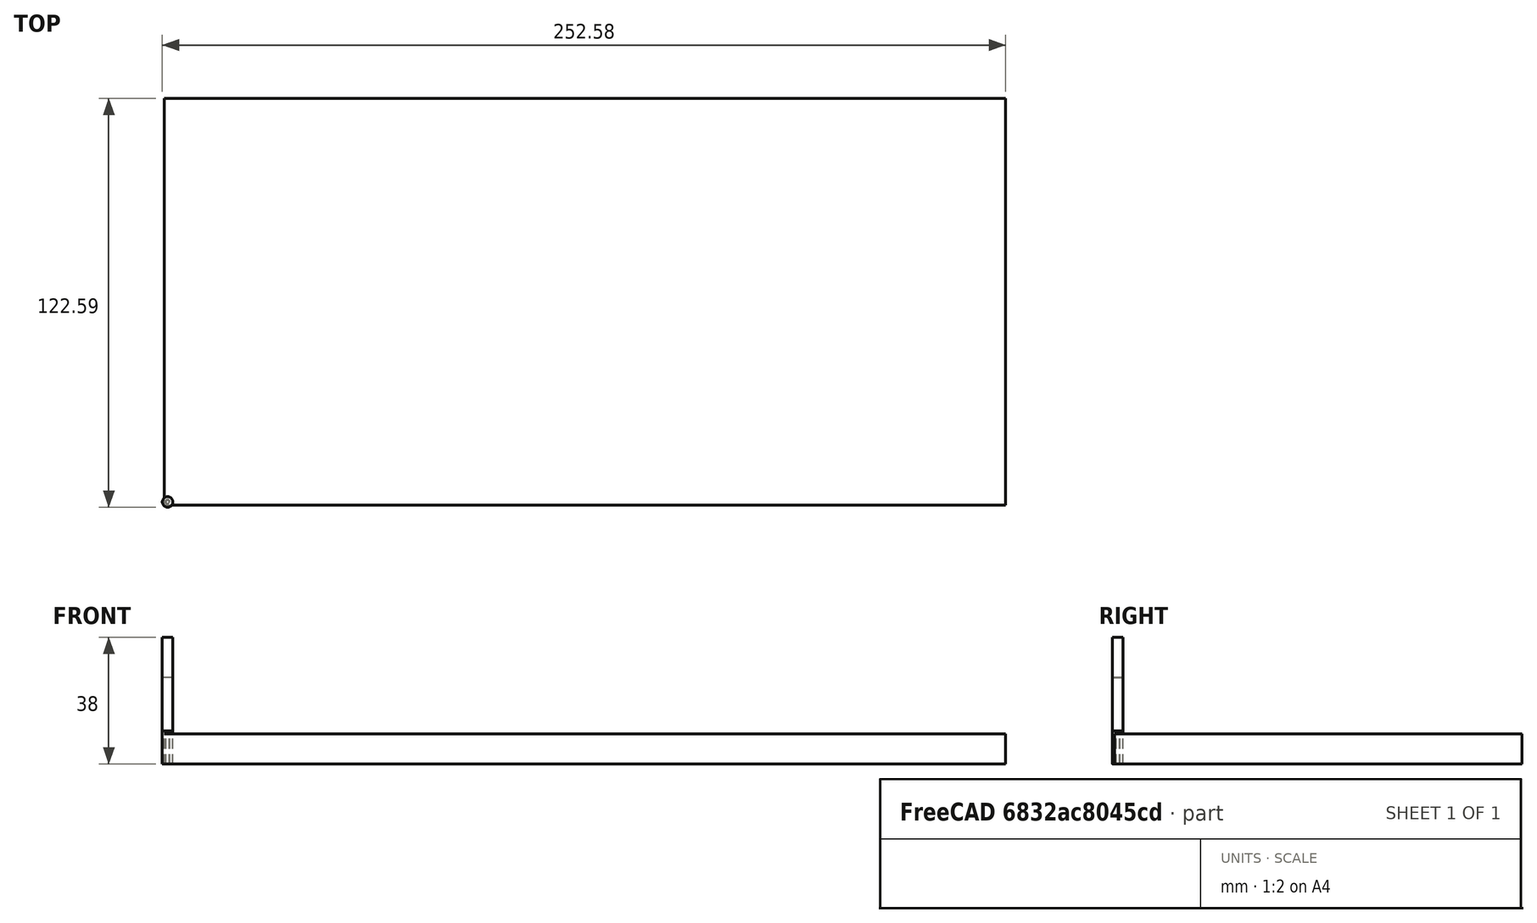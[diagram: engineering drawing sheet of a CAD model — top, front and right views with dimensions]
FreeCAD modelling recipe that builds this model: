
FCSTD DOCUMENT  (FreeCAD 0.21R33694 (Git))
Label: OIPT
License: Creative Commons Attribution 4.0
LicenseURL: https://creativecommons.org/licenses/by/4.0/
objects: Path::FeaturePython×22, Part::FeaturePython×20, App::DocumentObjectGroup×12, Part::Part2DObjectPython×4, Part::Extrusion×4, App::FeaturePython×4, Mesh::FeaturePython×2, PartDesign::AdditiveBox×1, PartDesign::SubtractiveBox×1, PartDesign::Body×1, Part::MultiFuse×1
note: 40 computed .brp shape members not serialized (recipe doc carries the construction recipe); baked Part::Feature solids carry a one-line shape summary decoded from their .brp

FEATURE [PartDesign::AdditiveBox] Box
  AttacherType = Attacher::AttachEngine3D
  Height = 9.1
  Length = 250
  MapMode = 5
  Support = -> [XY_Plane]
  Width = 120
FEATURE [Part::Part2DObjectPython] ShapeString  # Draft 2D object (typed FeaturePython)
  FontFile = /Library/Fonts/Arial Unicode.ttf
  Fuse = false
  Justification = 1
  JustificationReference = 0
  KeepLeftMargin = false
  MakeFace = true
  ObliqueAngle = 0
  Placement = pos=(43.8,91,7.1) rot=(0,0,1;0rad)
  ScaleToSize = true
  Size = 23
  String = ON PREMISE
  Tracking = 0
  expr: .Placement.Base.z = Box.Height - Box001.Height
FEATURE [Part::Part2DObjectPython] ShapeString001  # Draft 2D object (typed FeaturePython)
  FontFile = /Library/Fonts/Arial Unicode.ttf
  Fuse = false
  Justification = 1
  JustificationReference = 0
  KeepLeftMargin = false
  MakeFace = true
  ObliqueAngle = 0
  Placement = pos=(6.5,64,7.1) rot=(0,0,1;0rad)
  ScaleToSize = true
  Size = 23
  String = INFRASTRUCTURE
  Tracking = 0
  expr: .Placement.Base.z = Box.Height - Box001.Height
FEATURE [Part::Part2DObjectPython] ShapeString002  # Draft 2D object (typed FeaturePython)
  FontFile = /Library/Fonts/Arial Unicode.ttf
  Fuse = false
  Justification = 1
  JustificationReference = 0
  KeepLeftMargin = false
  MakeFace = true
  ObliqueAngle = 0
  Placement = pos=(52.45,37,7.1) rot=(0,0,1;0rad)
  ScaleToSize = true
  Size = 23
  String = PRODUCTS
  Tracking = 0
  expr: .Placement.Base.z = Box.Height - Box001.Height
FEATURE [PartDesign::SubtractiveBox] Box001
  AttacherType = Attacher::AttachEngine3D
  AttachmentOffset = pos=(5,5,-2) rot=(0,0,1;0rad)
  BaseFeature = -> Box
  Height = 2
  Length = 240
  MapMode = 5
  Placement = pos=(5,5,7.1) rot=(0,0,1;0rad)
  Support = -> [Box]
  Width = 110
  expr: .AttachmentOffset.Base.x = (Box.Length - Length) / 2
  expr: .AttachmentOffset.Base.y = (Box.Width - Width) / 2
  expr: .AttachmentOffset.Base.z = -Height
  expr: Length = Box.Length - 10 mm
  expr: Width = Box.Width - 10 mm
FEATURE [PartDesign::Body] Body
  Group = -> [Box,Box001]
  Origin = -> Origin
  Tip = -> Box001
FEATURE [Part::Part2DObjectPython] ShapeString003  # Draft 2D object (typed FeaturePython)
  FontFile = /Library/Fonts/Arial Unicode.ttf
  MakeFace = true
  Placement = pos=(81,12,7.1) rot=(-1e-06,0,1.00003;4e-06rad)
  Size = 23
  String = TEAM
  Tracking = 0
  expr: .Placement.Base.z = Box.Height - Box001.Height
FEATURE [Part::Extrusion] Extrude
  Base = -> ShapeString
  Dir = (0,0,1)
  DirMode = 2
  FaceMakerClass = Part::FaceMakerBullseye
  LengthFwd = 2
  LengthRev = 0
  Solid = true
  Symmetric = false
FEATURE [Part::Extrusion] Extrude001
  Base = -> ShapeString001
  Dir = (0,0,1)
  DirMode = 2
  FaceMakerClass = Part::FaceMakerBullseye
  LengthFwd = 2
  LengthRev = 0
  Solid = true
  Symmetric = false
FEATURE [Part::Extrusion] Extrude002
  Base = -> ShapeString002
  Dir = (0,0,1)
  DirMode = 2
  FaceMakerClass = Part::FaceMakerBullseye
  LengthFwd = 2
  LengthRev = 0
  Solid = true
  Symmetric = false
FEATURE [Part::Extrusion] Extrude003
  Base = -> ShapeString003
  Dir = (8.314e-13,2.7675e-12,1)
  DirMode = 2
  FaceMakerClass = Part::FaceMakerBullseye
  LengthFwd = 2
  LengthRev = 0
  Solid = true
  Symmetric = false
FEATURE [Part::MultiFuse] Fusion
  Shapes = -> [Body,Extrude,Extrude001,Extrude002,Extrude003]
FEATURE [App::FeaturePython] SetupSheet  # Path/CAM operation (typed FeaturePython)
  ClearanceHeightExpression = OpStockZMax+SetupSheet.ClearanceHeightOffset
  ClearanceHeightOffset = 5
  CoolantMode = 0
  CoolantModes = None | Flood | Mist
  FinalDepthExpression = OpFinalDepth
  HorizRapid = 0
  SafeHeightExpression = OpStockZMax+SetupSheet.SafeHeightOffset
  SafeHeightOffset = 3
  StartDepthExpression = OpStartDepth
  StepDownExpression = OpToolDiameter
  VertRapid = 0
FEATURE [Part::FeaturePython] Clone  label="Model-Fusion"  # Draft clone (typed FeaturePython)
  AttacherType = Attacher::AttachEngine3D
  Fuse = false
  Objects = -> [Fusion]
  PathResource = Model
  Scale = (1,1,1)
FEATURE [App::DocumentObjectGroup] Model
  Group = -> [Clone]
FEATURE [Part::FeaturePython] ToolBit  label="1.0mm-endmill"  # Path/CAM toolbit (typed FeaturePython)
  BitPropertyNames = Chipload | CuttingEdgeHeight | Diameter | Flutes | Length | Material | ShankDiameter | SpindleDirection
  BitShape = /Applications/FreeCAD.app/Contents/Resources/Mod/Path/Tools/Shape/endmill.fcstd
  Chipload = 0
  CuttingEdgeHeight = 10
  Diameter = 1
  Flutes = 0
  Length = 38
  Material = 0
  ShankDiameter = 3.17
  ShapeName = endmill
  SpindleDirection = 0
FEATURE [Path::FeaturePython] __0mm_endmill  label="1.0mm-endmill001"  # Path/CAM operation (typed FeaturePython)
  HorizFeed = 16.6667
  HorizRapid = 0
  SpindleDir = 0
  SpindleSpeed = 5000
  Tool = -> ToolBit
  ToolNumber = 5
  VertFeed = 16.6667
  VertRapid = 0
  expr: HorizRapid = SetupSheet.HorizRapid
  expr: VertRapid = SetupSheet.VertRapid
FEATURE [Part::FeaturePython] ToolBit001  label="1.4mm-endmill"  # Path/CAM toolbit (typed FeaturePython)
  BitPropertyNames = Chipload | CuttingEdgeHeight | Diameter | Flutes | Length | Material | ShankDiameter | SpindleDirection
  BitShape = /Applications/FreeCAD.app/Contents/Resources/Mod/Path/Tools/Shape/endmill.fcstd
  Chipload = 0
  CuttingEdgeHeight = 10
  Diameter = 1.4
  Flutes = 0
  Length = 26
  Material = 0
  ShankDiameter = 3
  ShapeName = endmill
  SpindleDirection = 0
FEATURE [Path::FeaturePython] __4mm_endmill  label="1.4mm-endmill001"  # Path/CAM operation (typed FeaturePython)
  HorizFeed = 16.6667
  HorizRapid = 0
  SpindleDir = 0
  SpindleSpeed = 10000
  Tool = -> ToolBit001
  ToolNumber = 2
  VertFeed = 16.6667
  VertRapid = 0
  expr: HorizRapid = SetupSheet.HorizRapid
  expr: VertRapid = SetupSheet.VertRapid
FEATURE [Part::FeaturePython] ToolBit002  label="3.175mm-endmill"  # Path/CAM toolbit (typed FeaturePython)
  BitPropertyNames = Chipload | CuttingEdgeHeight | Diameter | Flutes | Length | Material | ShankDiameter | SpindleDirection
  BitShape = /Applications/FreeCAD.app/Contents/Resources/Mod/Path/Tools/Shape/endmill.fcstd
  Chipload = 0
  CuttingEdgeHeight = 10
  Diameter = 3.17
  Flutes = 0
  Length = 26
  Material = 0
  ShankDiameter = 3
  ShapeName = endmill
  SpindleDirection = 0
FEATURE [Path::FeaturePython] __175mm_endmill  label="3.175mm-endmill001"  # Path/CAM operation (typed FeaturePython)
  HorizFeed = 16.6667
  HorizRapid = 0
  SpindleDir = 0
  SpindleSpeed = 10000
  Tool = -> ToolBit002
  ToolNumber = 4
  VertFeed = 16.6667
  VertRapid = 0
  expr: HorizRapid = SetupSheet.HorizRapid
  expr: VertRapid = SetupSheet.VertRapid
FEATURE [App::DocumentObjectGroup] Tools
  Group = -> [__0mm_endmill,__4mm_endmill,__175mm_endmill]
FEATURE [Part::FeaturePython] Stock  # WARN: FeaturePython — macro-defined, semantics opaque (R4)
  Base = -> Model
  ExtXneg = 1
  ExtXpos = 1
  ExtYneg = 1
  ExtYpos = 1
  ExtZneg = 0
  ExtZpos = 0
  StockType = FromBase
FEATURE [Path::FeaturePython] Pocket_Shape  # Path/CAM operation (typed FeaturePython)
  Active = true
  AreaParams:
    Tolerance = 1e-07
    FitArcs = True
    Simplify = False
    CleanDistance = 0.0
    Accuracy = 0.01
    Unit = 1.0
    MinArcPoints = 4
    MaxArcPoints = 100
    ClipperScale = 10000000.0
    Fill = 0
    Coplanar = 0
    Reorient = True
    Outline = False
    Explode = False
    OpenMode = 0
    Deflection = 0.01
    SubjectFill = 0
    ClipFill = 0
    Offset = 0.0
    ExtraPass = 0
    Stepover = 0.0
    LastStepover = 0.0
    JoinType = 0
    EndType = 0
    MiterLimit = 2.0
    RoundPrecision = 0.0
    PocketMode = 4
    ToolRadius = 1.585
    PocketExtraOffset = 0.0
    PocketStepover = 3.17
    PocketLastStepover = 0.0
    FromCenter = True
    Angle = 45.0
    AngleShift = 0.0
    Shift = 0.0
    Thicken = False
    SectionCount = -1
    Stepdown = 1.0
    SectionOffset = 0.0
    SectionTolerance = 1e-07
    SectionMode = 2
    Project = False
  Base = -> [Clone]
  ClearanceHeight = 14.1
  CoolantMode = 0
  CutMode = 0
  CycleTime = 00:27:07
  ExtensionCorners = true
  ExtensionLengthDefault = 1.585
  ExtraOffset = 0
  FinalDepth = 7.3
  FinishDepth = 0
  KeepToolDown = false
  MinTravel = false
  OffsetPattern = 2
  OpFinalDepth = 7.1
  OpStartDepth = 9.1
  OpStockZMax = 9.1
  OpStockZMin = 0
  OpToolDiameter = 3.17
  PathParams = {'orientation': 1, 'feedrate': 16.666666666666668, 'feedrate_v': 16.666666666666668, 'verbose': True, 'resume_height': 12.1, 'retraction': 14.1, 'return_end': True, 'preamble': False, 'start': Vector (217.01123131992824, 78.83016025976677, 14.1)}
  PocketLastStepOver = 0
  SafeHeight = 12.1
  SplitArcs = false
  StartAt = 0
  StartDepth = 9.3
  StartPoint = (0,0,0)
  StepDown = 1
  StepOver = 100
  ToolController = -> __175mm_endmill
  UseOutline = false
  UseStartPoint = false
  ZigZagAngle = 45
  expr: ClearanceHeight = OpStockZMax + SetupSheet.ClearanceHeightOffset
  expr: ExtensionLengthDefault = OpToolDiameter / 2
  expr: FinalDepth = 9.3 mm - Box001.Height
  expr: SafeHeight = OpStockZMax + SetupSheet.SafeHeightOffset
  expr: StartDepth = 9.3
  expr: StepDown = 1
FEATURE [App::DocumentObjectGroup] Operations
  Group = -> [Pocket_Shape]
FEATURE [Path::FeaturePython] Job  # Path/CAM operation (typed FeaturePython)
  CycleTime = 00:27:07
  Fixtures = G54
  GeometryTolerance = 0.01
  JobType = 0
  LastPostProcessDate = 2024-03-01 13:59:01.263896
  LastPostProcessOutput = /Volumes/NEW VOLUME/oipt1.nc
  Model = -> Model
  Operations = -> Operations
  OrderOutputBy = 0
  PostProcessor = 1
  PostProcessorOutputFile = <userpath>/3d_projects/CNC-stuff/placard/nameplate.nc
  SetupSheet = -> SetupSheet
  SplitOutput = false
  Stock = -> Stock
  Tools = -> Tools
FEATURE [Mesh::FeaturePython] CutMaterial  # WARN: FeaturePython — macro-defined, semantics opaque (R4)
FEATURE [App::FeaturePython] SetupSheet001  # Path/CAM operation (typed FeaturePython)
  ClearanceHeightExpression = OpStockZMax+SetupSheet001.ClearanceHeightOffset
  ClearanceHeightOffset = 5
  CoolantMode = 0
  CoolantModes = None | Flood | Mist
  FinalDepthExpression = OpFinalDepth
  HorizRapid = 0
  SafeHeightExpression = OpStockZMax+SetupSheet001.SafeHeightOffset
  SafeHeightOffset = 3
  StartDepthExpression = OpStartDepth
  StepDownExpression = OpToolDiameter
  VertRapid = 0
FEATURE [Part::FeaturePython] Clone001  label="Model-Fusion001"  # Draft clone (typed FeaturePython)
  AttacherType = Attacher::AttachEngine3D
  Fuse = false
  Objects = -> [Fusion]
  PathResource = Model
  Scale = (1,1,1)
FEATURE [App::DocumentObjectGroup] Model001
  Group = -> [Clone001]
FEATURE [Part::FeaturePython] ToolBit003  label="1.0mm-endmill003"  # Path/CAM toolbit (typed FeaturePython)
  BitPropertyNames = Chipload | CuttingEdgeHeight | Diameter | Flutes | Length | Material | ShankDiameter | SpindleDirection
  BitShape = /Applications/FreeCAD.app/Contents/Resources/Mod/Path/Tools/Shape/endmill.fcstd
  Chipload = 0
  CuttingEdgeHeight = 10
  Diameter = 1
  Flutes = 0
  Length = 38
  Material = 0
  ShankDiameter = 3.17
  ShapeName = endmill
  SpindleDirection = 0
FEATURE [Path::FeaturePython] __0mm_endmill001  label="1.0mm-endmill002"  # Path/CAM operation (typed FeaturePython)
  HorizFeed = 16.6667
  HorizRapid = 0
  SpindleDir = 0
  SpindleSpeed = 5000
  Tool = -> ToolBit003
  ToolNumber = 5
  VertFeed = 16.6667
  VertRapid = 0
  expr: HorizRapid = SetupSheet001.HorizRapid
  expr: VertRapid = SetupSheet001.VertRapid
FEATURE [Part::FeaturePython] ToolBit004  label="1.4mm-endmill003"  # Path/CAM toolbit (typed FeaturePython)
  BitPropertyNames = Chipload | CuttingEdgeHeight | Diameter | Flutes | Length | Material | ShankDiameter | SpindleDirection
  BitShape = /Applications/FreeCAD.app/Contents/Resources/Mod/Path/Tools/Shape/endmill.fcstd
  Chipload = 0
  CuttingEdgeHeight = 10
  Diameter = 1.4
  Flutes = 0
  Length = 26
  Material = 0
  ShankDiameter = 3
  ShapeName = endmill
  SpindleDirection = 0
FEATURE [Path::FeaturePython] __4mm_endmill001  label="1.4mm-endmill002"  # Path/CAM operation (typed FeaturePython)
  HorizFeed = 16.6667
  HorizRapid = 0
  SpindleDir = 0
  SpindleSpeed = 10000
  Tool = -> ToolBit004
  ToolNumber = 2
  VertFeed = 16.6667
  VertRapid = 0
  expr: HorizRapid = SetupSheet001.HorizRapid
  expr: VertRapid = SetupSheet001.VertRapid
FEATURE [Part::FeaturePython] ToolBit005  label="3.175mm-endmill003"  # Path/CAM toolbit (typed FeaturePython)
  BitPropertyNames = Chipload | CuttingEdgeHeight | Diameter | Flutes | Length | Material | ShankDiameter | SpindleDirection
  BitShape = /Applications/FreeCAD.app/Contents/Resources/Mod/Path/Tools/Shape/endmill.fcstd
  Chipload = 0
  CuttingEdgeHeight = 10
  Diameter = 3.17
  Flutes = 0
  Length = 26
  Material = 0
  ShankDiameter = 3
  ShapeName = endmill
  SpindleDirection = 0
FEATURE [Path::FeaturePython] __175mm_endmill001  label="3.175mm-endmill002"  # Path/CAM operation (typed FeaturePython)
  HorizFeed = 33.3333
  HorizRapid = 0
  SpindleDir = 0
  SpindleSpeed = 10000
  Tool = -> ToolBit005
  ToolNumber = 4
  VertFeed = 33.3333
  VertRapid = 0
  expr: HorizRapid = SetupSheet001.HorizRapid
  expr: VertRapid = SetupSheet001.VertRapid
FEATURE [App::DocumentObjectGroup] Tools001
  Group = -> [__0mm_endmill001,__4mm_endmill001,__175mm_endmill001]
FEATURE [Part::FeaturePython] Stock001  # WARN: FeaturePython — macro-defined, semantics opaque (R4)
  Base = -> Model001
  ExtXneg = 1
  ExtXpos = 1
  ExtYneg = 1
  ExtYpos = 1
  ExtZneg = 0
  ExtZpos = 0
  StockType = FromBase
FEATURE [Path::FeaturePython] Profile  # Path/CAM operation (typed FeaturePython)
  Active = true
  AreaParams:
    Tolerance = 1e-07
    FitArcs = True
    Simplify = False
    CleanDistance = 0.0
    Accuracy = 0.01
    Unit = 1.0
    MinArcPoints = 4
    MaxArcPoints = 100
    ClipperScale = 10000000.0
    Fill = 0
    Coplanar = 0
    Reorient = True
    Outline = False
    Explode = False
    OpenMode = 0
    Deflection = 0.01
    SubjectFill = 0
    ClipFill = 0
    Offset = 0.7
    ExtraPass = 0
    Stepover = 0.0
    LastStepover = 0.0
    JoinType = 0
    EndType = 0
    MiterLimit = 2.0
    RoundPrecision = 0.0
    PocketMode = 0
    ToolRadius = 1.0
    PocketExtraOffset = 0.0
    PocketStepover = 0.0
    PocketLastStepover = 0.0
    FromCenter = False
    Angle = 45.0
    AngleShift = 0.0
    Shift = 0.0
    Thicken = False
    SectionCount = -1
    Stepdown = 1.0
    SectionOffset = 0.0
    SectionTolerance = 1e-07
    SectionMode = 2
    Project = False
  Base = -> [Clone001]
  ClearanceHeight = 14.1
  CoolantMode = 0
  CycleTime = 00:04:38
  Direction = 0
  FinalDepth = 7.1
  HandleMultipleFeatures = 0
  JoinType = 0
  MiterLimit = 0.1
  OffsetExtra = 0
  OpFinalDepth = 7.1
  OpStartDepth = 9.1
  OpStockZMax = 9.1
  OpStockZMin = 0
  OpToolDiameter = 1.4
  PathParams = {'orientation': 0, 'feedrate': 16.666666666666668, 'feedrate_v': 16.666666666666668, 'verbose': True, 'resume_height': 12.1, 'retraction': 14.1, 'return_end': True, 'preamble': False, 'start': Vector (112.09030395670032, 21.42941604003683, 14.1)}
  SafeHeight = 12.1
  Side = 1
  SplitArcs = false
  StartDepth = 7.1
  StartPoint = (0,0,0)
  StepDown = 1.4
  ToolController = -> __4mm_endmill001
  UseComp = true
  UseStartPoint = false
  processCircles = true
  processHoles = true
  processPerimeter = true
  expr: ClearanceHeight = OpStockZMax + SetupSheet001.ClearanceHeightOffset
  expr: FinalDepth = Box.Height - Box001.Height
  expr: SafeHeight = OpStockZMax + SetupSheet001.SafeHeightOffset
  expr: StartDepth = Box.Height - Box001.Height
  expr: StepDown = OpToolDiameter
FEATURE [Path::FeaturePython] Profile001  # Path/CAM operation (typed FeaturePython)
  Active = true
  AreaParams:
    Tolerance = 1e-07
    FitArcs = True
    Simplify = False
    CleanDistance = 0.0
    Accuracy = 0.01
    Unit = 1.0
    MinArcPoints = 4
    MaxArcPoints = 100
    ClipperScale = 10000000.0
    Fill = 0
    Coplanar = 0
    Reorient = True
    Outline = False
    Explode = False
    OpenMode = 0
    Deflection = 0.01
    SubjectFill = 0
    ClipFill = 0
    Offset = -0.7
    ExtraPass = 0
    Stepover = 0.0
    LastStepover = 0.0
    JoinType = 0
    EndType = 0
    MiterLimit = 2.0
    RoundPrecision = 0.0
    PocketMode = 0
    ToolRadius = 1.0
    PocketExtraOffset = 0.0
    PocketStepover = 0.0
    PocketLastStepover = 0.0
    FromCenter = False
    Angle = 45.0
    AngleShift = 0.0
    Shift = 0.0
    Thicken = False
    SectionCount = -1
    Stepdown = 1.0
    SectionOffset = 0.0
    SectionTolerance = 1e-07
    SectionMode = 2
    Project = False
  Base = -> [Clone001]
  ClearanceHeight = 14.1
  CoolantMode = 0
  CycleTime = 00:00:59
  Direction = 0
  FinalDepth = 7.1
  HandleMultipleFeatures = 0
  JoinType = 0
  MiterLimit = 0.1
  OffsetExtra = 0
  OpFinalDepth = 7.1
  OpStartDepth = 9.1
  OpStockZMax = 9.1
  OpStockZMin = 0
  OpToolDiameter = 1.4
  PathParams = {'orientation': 1, 'feedrate': 16.666666666666668, 'feedrate_v': 16.666666666666668, 'verbose': True, 'resume_height': 12.1, 'retraction': 14.1, 'return_end': True, 'preamble': False}
  SafeHeight = 12.1
  Side = 1
  SplitArcs = false
  StartDepth = 7.1
  StartPoint = (0,0,0)
  StepDown = 1.4
  ToolController = -> __4mm_endmill001
  UseComp = true
  UseStartPoint = false
  processCircles = true
  processHoles = true
  processPerimeter = true
  expr: ClearanceHeight = OpStockZMax + SetupSheet001.ClearanceHeightOffset
  expr: FinalDepth = Box.Height - Box001.Height
  expr: SafeHeight = OpStockZMax + SetupSheet001.SafeHeightOffset
  expr: StartDepth = Box.Height - Box001.Height
  expr: StepDown = OpToolDiameter
FEATURE [App::DocumentObjectGroup] Operations001
  Group = -> [Profile,Profile001]
FEATURE [Path::FeaturePython] Job001  # Path/CAM operation (typed FeaturePython)
  CycleTime = 00:05:37
  Fixtures = G54
  GeometryTolerance = 0.01
  JobType = 0
  Model = -> Model001
  Operations = -> Operations001
  OrderOutputBy = 0
  PostProcessor = 1
  PostProcessorOutputFile = <userpath>/3d_projects/CNC-stuff/placard/nameplate.nc
  SetupSheet = -> SetupSheet001
  SplitOutput = false
  Stock = -> Stock001
  Tools = -> Tools001
FEATURE [App::FeaturePython] SetupSheet002  # Path/CAM operation (typed FeaturePython)
  ClearanceHeightExpression = OpStockZMax+SetupSheet002.ClearanceHeightOffset
  ClearanceHeightOffset = 5
  CoolantMode = 0
  CoolantModes = None | Flood | Mist
  FinalDepthExpression = OpFinalDepth
  HorizRapid = 0
  SafeHeightExpression = OpStockZMax+SetupSheet002.SafeHeightOffset
  SafeHeightOffset = 3
  StartDepthExpression = OpStartDepth
  StepDownExpression = OpToolDiameter
  VertRapid = 0
FEATURE [Part::FeaturePython] Clone002  label="Model-Fusion002"  # Draft clone (typed FeaturePython)
  AttacherType = Attacher::AttachEngine3D
  Fuse = false
  Objects = -> [Fusion]
  PathResource = Model
  Scale = (1,1,1)
FEATURE [App::DocumentObjectGroup] Model002
  Group = -> [Clone002]
FEATURE [Part::FeaturePython] ToolBit006  label="1.0mm-endmill005"  # Path/CAM toolbit (typed FeaturePython)
  BitPropertyNames = Chipload | CuttingEdgeHeight | Diameter | Flutes | Length | Material | ShankDiameter | SpindleDirection
  BitShape = /Applications/FreeCAD.app/Contents/Resources/Mod/Path/Tools/Shape/endmill.fcstd
  Chipload = 0
  CuttingEdgeHeight = 10
  Diameter = 1
  Flutes = 0
  Length = 38
  Material = 0
  ShankDiameter = 3.17
  ShapeName = endmill
  SpindleDirection = 0
FEATURE [Path::FeaturePython] __0mm_endmill002  label="1.0mm-endmill004"  # Path/CAM operation (typed FeaturePython)
  HorizFeed = 16.6667
  HorizRapid = 0
  SpindleDir = 0
  SpindleSpeed = 5000
  Tool = -> ToolBit006
  ToolNumber = 5
  VertFeed = 16.6667
  VertRapid = 0
  expr: HorizRapid = SetupSheet002.HorizRapid
  expr: VertRapid = SetupSheet002.VertRapid
FEATURE [Part::FeaturePython] ToolBit007  label="1.4mm-endmill005"  # Path/CAM toolbit (typed FeaturePython)
  BitPropertyNames = Chipload | CuttingEdgeHeight | Diameter | Flutes | Length | Material | ShankDiameter | SpindleDirection
  BitShape = /Applications/FreeCAD.app/Contents/Resources/Mod/Path/Tools/Shape/endmill.fcstd
  Chipload = 0
  CuttingEdgeHeight = 10
  Diameter = 1.4
  Flutes = 0
  Length = 26
  Material = 0
  ShankDiameter = 3
  ShapeName = endmill
  SpindleDirection = 0
FEATURE [Path::FeaturePython] __4mm_endmill002  label="1.4mm-endmill004"  # Path/CAM operation (typed FeaturePython)
  HorizFeed = 16.6667
  HorizRapid = 0
  SpindleDir = 0
  SpindleSpeed = 10000
  Tool = -> ToolBit007
  ToolNumber = 2
  VertFeed = 16.6667
  VertRapid = 0
  expr: HorizRapid = SetupSheet002.HorizRapid
  expr: VertRapid = SetupSheet002.VertRapid
FEATURE [Part::FeaturePython] ToolBit008  label="3.175mm-endmill005"  # Path/CAM toolbit (typed FeaturePython)
  BitPropertyNames = Chipload | CuttingEdgeHeight | Diameter | Flutes | Length | Material | ShankDiameter | SpindleDirection
  BitShape = /Applications/FreeCAD.app/Contents/Resources/Mod/Path/Tools/Shape/endmill.fcstd
  Chipload = 0
  CuttingEdgeHeight = 10
  Diameter = 3.17
  Flutes = 0
  Length = 26
  Material = 0
  ShankDiameter = 3
  ShapeName = endmill
  SpindleDirection = 0
FEATURE [Path::FeaturePython] __175mm_endmill002  label="3.175mm-endmill004"  # Path/CAM operation (typed FeaturePython)
  HorizFeed = 33.3333
  HorizRapid = 0
  SpindleDir = 0
  SpindleSpeed = 10000
  Tool = -> ToolBit008
  ToolNumber = 4
  VertFeed = 33.3333
  VertRapid = 0
  expr: HorizRapid = SetupSheet002.HorizRapid
  expr: VertRapid = SetupSheet002.VertRapid
FEATURE [App::DocumentObjectGroup] Tools002
  Group = -> [__0mm_endmill002,__4mm_endmill002,__175mm_endmill002]
FEATURE [Part::FeaturePython] Stock002  # WARN: FeaturePython — macro-defined, semantics opaque (R4)
  Base = -> Model002
  ExtXneg = 1
  ExtXpos = 1
  ExtYneg = 1
  ExtYpos = 1
  ExtZneg = 0
  ExtZpos = 0
  StockType = FromBase
FEATURE [Path::FeaturePython] Profile002  # Path/CAM operation (typed FeaturePython)
  Active = true
  AreaParams:
    Tolerance = 1e-07
    FitArcs = True
    Simplify = False
    CleanDistance = 0.0
    Accuracy = 0.01
    Unit = 1.0
    MinArcPoints = 4
    MaxArcPoints = 100
    ClipperScale = 10000000.0
    Fill = 0
    Coplanar = 0
    Reorient = True
    Outline = False
    Explode = False
    OpenMode = 0
    Deflection = 0.01
    SubjectFill = 0
    ClipFill = 0
    Offset = 0.5
    ExtraPass = 0
    Stepover = 0.0
    LastStepover = 0.0
    JoinType = 0
    EndType = 0
    MiterLimit = 2.0
    RoundPrecision = 0.0
    PocketMode = 0
    ToolRadius = 1.0
    PocketExtraOffset = 0.0
    PocketStepover = 0.0
    PocketLastStepover = 0.0
    FromCenter = False
    Angle = 45.0
    AngleShift = 0.0
    Shift = 0.0
    Thicken = False
    SectionCount = -1
    Stepdown = 1.0
    SectionOffset = 0.0
    SectionTolerance = 1e-07
    SectionMode = 2
    Project = False
  Base = -> [Clone002]
  ClearanceHeight = 14.1
  CoolantMode = 0
  CycleTime = 00:04:38
  Direction = 0
  FinalDepth = 7.1
  HandleMultipleFeatures = 0
  JoinType = 0
  MiterLimit = 0.1
  OffsetExtra = 0
  OpFinalDepth = 7.1
  OpStartDepth = 9.1
  OpStockZMax = 9.1
  OpStockZMin = 0
  OpToolDiameter = 1
  PathParams = {'orientation': 0, 'feedrate': 16.666666666666668, 'feedrate_v': 16.666666666666668, 'verbose': True, 'resume_height': 12.1, 'retraction': 14.1, 'return_end': True, 'preamble': False, 'start': Vector (111.89030443104416, 21.313495172891262, 14.1)}
  SafeHeight = 12.1
  Side = 1
  SplitArcs = false
  StartDepth = 7.1
  StartPoint = (0,0,0)
  StepDown = 1
  ToolController = -> __0mm_endmill002
  UseComp = true
  UseStartPoint = false
  processCircles = true
  processHoles = true
  processPerimeter = true
  expr: ClearanceHeight = OpStockZMax + SetupSheet002.ClearanceHeightOffset
  expr: FinalDepth = Box.Height - Box001.Height
  expr: SafeHeight = OpStockZMax + SetupSheet002.SafeHeightOffset
  expr: StartDepth = Box.Height - Box001.Height
  expr: StepDown = OpToolDiameter
FEATURE [Path::FeaturePython] Profile003  # Path/CAM operation (typed FeaturePython)
  Active = true
  AreaParams:
    Tolerance = 1e-07
    FitArcs = True
    Simplify = False
    CleanDistance = 0.0
    Accuracy = 0.01
    Unit = 1.0
    MinArcPoints = 4
    MaxArcPoints = 100
    ClipperScale = 10000000.0
    Fill = 0
    Coplanar = 0
    Reorient = True
    Outline = False
    Explode = False
    OpenMode = 0
    Deflection = 0.01
    SubjectFill = 0
    ClipFill = 0
    Offset = -0.5
    ExtraPass = 0
    Stepover = 0.0
    LastStepover = 0.0
    JoinType = 0
    EndType = 0
    MiterLimit = 2.0
    RoundPrecision = 0.0
    PocketMode = 0
    ToolRadius = 1.0
    PocketExtraOffset = 0.0
    PocketStepover = 0.0
    PocketLastStepover = 0.0
    FromCenter = False
    Angle = 45.0
    AngleShift = 0.0
    Shift = 0.0
    Thicken = False
    SectionCount = -1
    Stepdown = 1.0
    SectionOffset = 0.0
    SectionTolerance = 1e-07
    SectionMode = 2
    Project = False
  Base = -> [Clone002]
  ClearanceHeight = 14.1
  CoolantMode = 0
  CycleTime = 00:00:59
  Direction = 0
  FinalDepth = 7.1
  HandleMultipleFeatures = 0
  JoinType = 0
  MiterLimit = 0.1
  OffsetExtra = 0
  OpFinalDepth = 7.1
  OpStartDepth = 9.1
  OpStockZMax = 9.1
  OpStockZMin = 0
  OpToolDiameter = 1
  PathParams = {'orientation': 1, 'feedrate': 16.666666666666668, 'feedrate_v': 16.666666666666668, 'verbose': True, 'resume_height': 12.1, 'retraction': 14.1, 'return_end': True, 'preamble': False}
  SafeHeight = 12.1
  Side = 1
  SplitArcs = false
  StartDepth = 7.1
  StartPoint = (0,0,0)
  StepDown = 1
  ToolController = -> __0mm_endmill002
  UseComp = true
  UseStartPoint = false
  processCircles = false
  processHoles = false
  processPerimeter = true
  expr: ClearanceHeight = OpStockZMax + SetupSheet002.ClearanceHeightOffset
  expr: FinalDepth = Box.Height - Box001.Height
  expr: SafeHeight = OpStockZMax + SetupSheet002.SafeHeightOffset
  expr: StartDepth = Box.Height - Box001.Height
  expr: StepDown = OpToolDiameter
FEATURE [App::DocumentObjectGroup] Operations002
  Group = -> [Profile002,Profile003]
FEATURE [Path::FeaturePython] Job002  # Path/CAM operation (typed FeaturePython)
  CycleTime = 00:05:37
  Fixtures = G54
  GeometryTolerance = 0.01
  JobType = 0
  Model = -> Model002
  Operations = -> Operations002
  OrderOutputBy = 0
  PostProcessor = 1
  PostProcessorOutputFile = <userpath>/3d_projects/CNC-stuff/placard/nameplate.nc
  SetupSheet = -> SetupSheet002
  SplitOutput = false
  Stock = -> Stock002
  Tools = -> Tools002
FEATURE [App::FeaturePython] SetupSheet003  # Path/CAM operation (typed FeaturePython)
  ClearanceHeightExpression = OpStockZMax+SetupSheet003.ClearanceHeightOffset
  ClearanceHeightOffset = 5
  CoolantMode = 0
  CoolantModes = None | Flood | Mist
  FinalDepthExpression = OpFinalDepth
  HorizRapid = 0
  SafeHeightExpression = OpStockZMax+SetupSheet003.SafeHeightOffset
  SafeHeightOffset = 3
  StartDepthExpression = OpStartDepth
  StepDownExpression = OpToolDiameter
  VertRapid = 0
FEATURE [Part::FeaturePython] Clone003  label="Model-Fusion003"  # Draft clone (typed FeaturePython)
  AttacherType = Attacher::AttachEngine3D
  Fuse = false
  Objects = -> [Fusion]
  PathResource = Model
  Scale = (1,1,1)
FEATURE [App::DocumentObjectGroup] Model003
  Group = -> [Clone003]
FEATURE [Part::FeaturePython] ToolBit009  label="0.8mm-endmill"  # Path/CAM toolbit (typed FeaturePython)
  BitPropertyNames = Chipload | CuttingEdgeHeight | Diameter | Flutes | Length | Material | ShankDiameter | SpindleDirection
  BitShape = /Applications/FreeCAD.app/Contents/Resources/Mod/Path/Tools/Shape/endmill.fcstd
  Chipload = 0
  CuttingEdgeHeight = 10
  Diameter = 0.8
  Flutes = 0
  Length = 26
  Material = 0
  ShankDiameter = 3
  ShapeName = endmill
  SpindleDirection = 0
FEATURE [Path::FeaturePython] __8mm_endmill  label="0.8mm-endmill001"  # Path/CAM operation (typed FeaturePython)
  HorizFeed = 16.6667
  HorizRapid = 0
  SpindleDir = 0
  SpindleSpeed = 10000
  Tool = -> ToolBit009
  ToolNumber = 3
  VertFeed = 16.6667
  VertRapid = 0
  expr: HorizRapid = SetupSheet003.HorizRapid
  expr: VertRapid = SetupSheet003.VertRapid
FEATURE [Part::FeaturePython] ToolBit010  label="1.4mm-endmill007"  # Path/CAM toolbit (typed FeaturePython)
  BitPropertyNames = Chipload | CuttingEdgeHeight | Diameter | Flutes | Length | Material | ShankDiameter | SpindleDirection
  BitShape = /Applications/FreeCAD.app/Contents/Resources/Mod/Path/Tools/Shape/endmill.fcstd
  Chipload = 0
  CuttingEdgeHeight = 10
  Diameter = 1.4
  Flutes = 0
  Length = 26
  Material = 0
  ShankDiameter = 3
  ShapeName = endmill
  SpindleDirection = 0
FEATURE [Path::FeaturePython] __4mm_endmill003  label="1.4mm-endmill006"  # Path/CAM operation (typed FeaturePython)
  HorizFeed = 16.6667
  HorizRapid = 0
  SpindleDir = 0
  SpindleSpeed = 10000
  Tool = -> ToolBit010
  ToolNumber = 2
  VertFeed = 16.6667
  VertRapid = 0
  expr: HorizRapid = SetupSheet003.HorizRapid
  expr: VertRapid = SetupSheet003.VertRapid
FEATURE [Part::FeaturePython] ToolBit011  label="3.175mm-endmill007"  # Path/CAM toolbit (typed FeaturePython)
  BitPropertyNames = Chipload | CuttingEdgeHeight | Diameter | Flutes | Length | Material | ShankDiameter | SpindleDirection
  BitShape = /Applications/FreeCAD.app/Contents/Resources/Mod/Path/Tools/Shape/endmill.fcstd
  Chipload = 0
  CuttingEdgeHeight = 10
  Diameter = 3.17
  Flutes = 0
  Length = 26
  Material = 0
  ShankDiameter = 3
  ShapeName = endmill
  SpindleDirection = 0
FEATURE [Path::FeaturePython] __175mm_endmill003  label="3.175mm-endmill006"  # Path/CAM operation (typed FeaturePython)
  HorizFeed = 3.33333
  HorizRapid = 0
  SpindleDir = 0
  SpindleSpeed = 400
  Tool = -> ToolBit011
  ToolNumber = 4
  VertFeed = 3.33333
  VertRapid = 0
  expr: HorizRapid = SetupSheet003.HorizRapid
  expr: VertRapid = SetupSheet003.VertRapid
FEATURE [App::DocumentObjectGroup] Tools003
  Group = -> [__8mm_endmill,__4mm_endmill003,__175mm_endmill003]
FEATURE [Part::FeaturePython] Stock003  # WARN: FeaturePython — macro-defined, semantics opaque (R4)
  Base = -> Model003
  ExtXneg = 1
  ExtXpos = 1
  ExtYneg = 1
  ExtYpos = 1
  ExtZneg = 0
  ExtZpos = 0
  StockType = FromBase
FEATURE [Path::FeaturePython] MillFace  # Path/CAM operation (typed FeaturePython)
  Active = true
  AreaParams:
    Tolerance = 1e-07
    FitArcs = True
    Simplify = False
    CleanDistance = 0.0
    Accuracy = 0.01
    Unit = 1.0
    MinArcPoints = 4
    MaxArcPoints = 100
    ClipperScale = 10000000.0
    Fill = 0
    Coplanar = 0
    Reorient = True
    Outline = False
    Explode = False
    OpenMode = 0
    Deflection = 0.01
    SubjectFill = 0
    ClipFill = 0
    Offset = 0.0
    ExtraPass = 0
    Stepover = 0.0
    LastStepover = 0.0
    JoinType = 0
    EndType = 0
    MiterLimit = 2.0
    RoundPrecision = 0.0
    PocketMode = 4
    ToolRadius = 1.585
    PocketExtraOffset = 0.0
    PocketStepover = 0.7925
    PocketLastStepover = 0.0
    FromCenter = True
    Angle = 45.0
    AngleShift = 0.0
    Shift = 0.0
    Thicken = False
    SectionCount = -1
    Stepdown = 1.0
    SectionOffset = 0.0
    SectionTolerance = 1e-07
    SectionMode = 2
    Project = False
  Base = -> [Clone003]
  BoundaryShape = 3
  ClearEdges = false
  ClearanceHeight = 14.1
  CoolantMode = 0
  CutMode = 0
  CycleTime = 09:38:27
  ExcludeRaisedAreas = false
  ExtraOffset = 0
  FinalDepth = 8.8
  FinishDepth = 0
  KeepToolDown = false
  MinTravel = false
  OffsetPattern = 2
  OpFinalDepth = 9.1
  OpStartDepth = 9.2
  OpStockZMax = 9.1
  OpStockZMin = 0
  OpToolDiameter = 3.17
  PathParams = {'orientation': 1, 'feedrate': 3.3333333333333335, 'feedrate_v': 3.3333333333333335, 'verbose': True, 'resume_height': 12.1, 'retraction': 14.1, 'return_end': True, 'preamble': False}
  PocketLastStepOver = 0
  SafeHeight = 12.1
  SplitArcs = false
  StartAt = 0
  StartDepth = 9.1
  StartPoint = (0,0,0)
  StepDown = 0.1
  StepOver = 25
  ToolController = -> __175mm_endmill003
  UseStartPoint = false
  ZigZagAngle = 45
  expr: ClearanceHeight = OpStockZMax + SetupSheet003.ClearanceHeightOffset
  expr: FinalDepth = Box.Height - 0.3 mm
  expr: SafeHeight = OpStockZMax + SetupSheet003.SafeHeightOffset
  expr: StartDepth = Box.Height
  expr: StepDown = 0.1
FEATURE [App::DocumentObjectGroup] Operations003
  Group = -> [MillFace]
FEATURE [Path::FeaturePython] Job003  # Path/CAM operation (typed FeaturePython)
  CycleTime = 09:38:27
  Fixtures = G54
  GeometryTolerance = 0.01
  JobType = 0
  Model = -> Model003
  Operations = -> Operations003
  OrderOutputBy = 0
  PostProcessor = 1
  PostProcessorOutputFile = <userpath>/3d_projects/CNC-stuff/placard/nameplate.nc
  SetupSheet = -> SetupSheet003
  SplitOutput = false
  Stock = -> Stock003
  Tools = -> Tools003
FEATURE [Mesh::FeaturePython] CutMaterial001  # WARN: FeaturePython — macro-defined, semantics opaque (R4)
